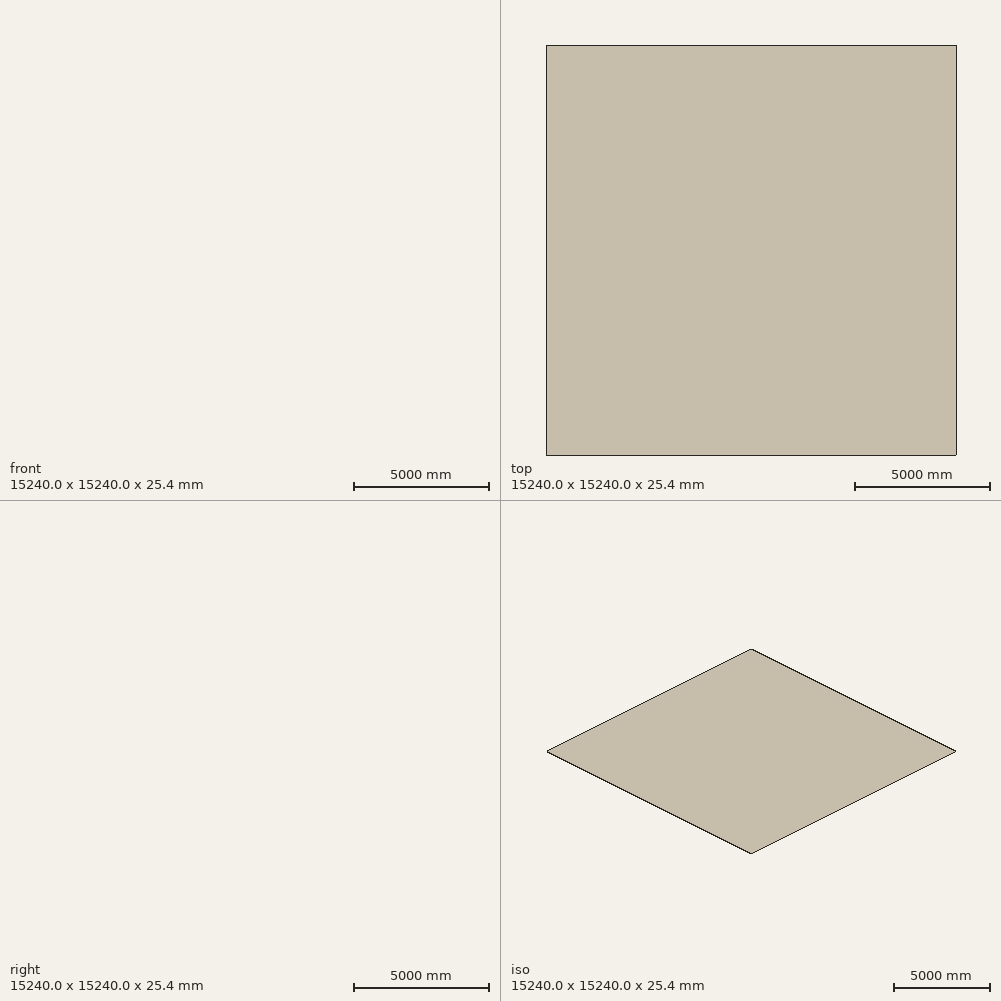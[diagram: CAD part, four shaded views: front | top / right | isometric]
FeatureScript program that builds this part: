
annotation { "Feature Type Name" : "Feature", "Feature Type Description" : "" }
export const myFeature = defineFeature(function(context is Context, id is Id, definition is map)
    precondition{}
    {
        {
            var Q0;
            Q0=qCreatedBy(makeId("Top.planeOp"),FACE);
            var sketch = newSketch(context, id + "F0", { "sketchPlane" : qUnion([Q0])});
            skLineSegment(sketch, "E0.bottom", {"start": v(-7665.34, -7620) * mm, "end": v(7574.66, -7620) * mm});
            skLineSegment(sketch, "E0.top", {"start": v(-7665.34, 7620) * mm, "end": v(7574.66, 7620) * mm});
            skLineSegment(sketch, "E0.left", {"start": v(-7665.34, -7620) * mm, "end": v(-7665.34, 7620) * mm});
            skLineSegment(sketch, "E0.right", {"start": v(7574.66, -7620) * mm, "end": v(7574.66, 7620) * mm});
            skPoint(sketch, "E0.middle", {"position": v(-45.34, 0) * mm});
            skSolve(sketch);
        }
        {
            var Q0;
            Q0=makeQuery(id+"F0.imprint","IMPRINT",FACE,{"disambiguationData":[TD([[makeQuery(id+"F0.imprint","IMPRINT",EDGE,{"derivedFrom":sQuery(id+"F0.wireOp",EDGE,"E0.bottom")}),1.0]])]});
            extrude(context, id + "F1", {"entities" : qUnion([Q0]), "depth" : 25.4 * mm});
        }
    });
